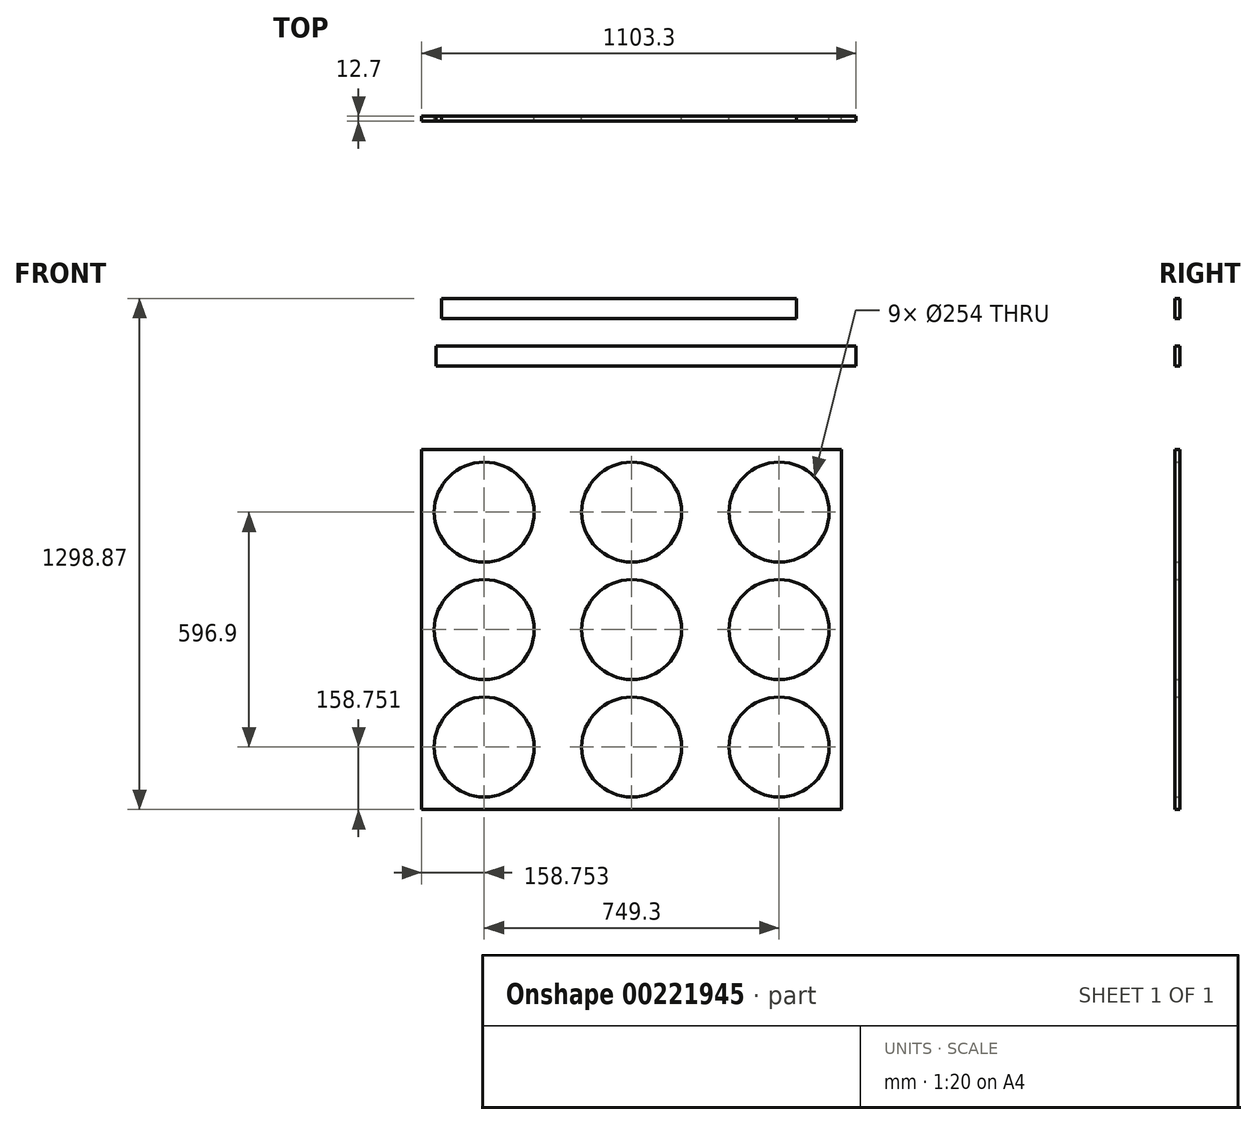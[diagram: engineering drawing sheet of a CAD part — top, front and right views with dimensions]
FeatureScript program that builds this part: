
annotation { "Feature Type Name" : "Feature", "Feature Type Description" : "" }
export const myFeature = defineFeature(function(context is Context, id is Id, definition is map)
    precondition{}
    {
        {
            var Q0;
            Q0=qCreatedBy(makeId("Front.planeOp"),FACE);
            var sketch = newSketch(context, id + "F0", { "sketchPlane" : qUnion([Q0])});
            skLineSegment(sketch, "E0.bottom", {"start": v(-474.18, 572.11) * mm, "end": v(592.62, 572.11) * mm});
            skLineSegment(sketch, "E0.top", {"start": v(-474.18, -342.29) * mm, "end": v(592.62, -342.29) * mm});
            skLineSegment(sketch, "E0.left", {"start": v(-474.18, 572.11) * mm, "end": v(-474.18, -342.29) * mm});
            skLineSegment(sketch, "E0.right", {"start": v(592.62, 572.11) * mm, "end": v(592.62, -342.29) * mm});
            skLineSegment(sketch, "E1.0", {"start": v(-474.18, -183.54) * mm, "end": v(440.22, -183.54) * mm, "construction": true});
            skLineSegment(sketch, "E2.0", {"start": v(-315.43, 572.11) * mm, "end": v(-315.43, -342.29) * mm, "construction": true});
            skLineSegment(sketch, "E3.0", {"start": v(433.87, 572.11) * mm, "end": v(433.87, -342.29) * mm, "construction": true});
            skLineSegment(sketch, "E4.0", {"start": v(-474.18, 114.91) * mm, "end": v(440.22, 114.91) * mm, "construction": true});
            skLineSegment(sketch, "E5.0", {"start": v(59.22, 572.11) * mm, "end": v(59.22, -342.29) * mm, "construction": true});
            skCircle(sketch, "E6", {"center": v(-315.43, 114.91) * mm, "radius": 127 * mm});
            skCircle(sketch, "E7", {"center": v(-315.43, -183.54) * mm, "radius": 127 * mm});
            skCircle(sketch, "E8", {"center": v(433.87, -183.54) * mm, "radius": 127 * mm});
            skCircle(sketch, "E9", {"center": v(433.87, 114.91) * mm, "radius": 127 * mm});
            skLineSegment(sketch, "E10.0", {"start": v(-474.18, 413.36) * mm, "end": v(440.22, 413.36) * mm, "construction": true});
            skCircle(sketch, "E11", {"center": v(-315.43, 413.36) * mm, "radius": 127 * mm});
            skCircle(sketch, "E12", {"center": v(433.87, 413.36) * mm, "radius": 127 * mm});
            skCircle(sketch, "E13", {"center": v(59.22, 413.36) * mm, "radius": 127 * mm});
            skCircle(sketch, "E14", {"center": v(59.22, 114.91) * mm, "radius": 127 * mm});
            skCircle(sketch, "E15", {"center": v(59.22, -183.54) * mm, "radius": 127 * mm});
            skSolve(sketch);
        }
        {
            var Q0;
            Q0=makeQuery(id+"F0.imprint","IMPRINT",FACE,{"disambiguationData":[TD([[makeQuery(id+"F0.imprint","IMPRINT",EDGE,{"derivedFrom":sQuery(id+"F0.wireOp",EDGE,"E0.bottom")}),-1.0]])]});
            extrude(context, id + "F1", {"entities" : qUnion([Q0]), "depth" : 12.7 * mm});
        }
        {
            var Q0;
            Q0=qCreatedBy(makeId("Front.planeOp"),FACE);
            var sketch = newSketch(context, id + "F2", { "sketchPlane" : qUnion([Q0])});
            skLineSegment(sketch, "E16.bottom", {"start": v(-437.68, 835.84) * mm, "end": v(629.12, 835.84) * mm});
            skLineSegment(sketch, "E16.top", {"start": v(-437.68, 785.04) * mm, "end": v(629.12, 785.04) * mm});
            skLineSegment(sketch, "E16.left", {"start": v(-437.68, 835.84) * mm, "end": v(-437.68, 785.04) * mm});
            skLineSegment(sketch, "E16.right", {"start": v(629.12, 835.84) * mm, "end": v(629.12, 785.04) * mm});
            skLineSegment(sketch, "E17.bottom", {"start": v(-423.4, 956.58) * mm, "end": v(478.3, 956.58) * mm});
            skLineSegment(sketch, "E17.top", {"start": v(-423.4, 905.78) * mm, "end": v(478.3, 905.78) * mm});
            skLineSegment(sketch, "E17.left", {"start": v(-423.4, 956.58) * mm, "end": v(-423.4, 905.78) * mm});
            skLineSegment(sketch, "E17.right", {"start": v(478.3, 956.58) * mm, "end": v(478.3, 905.78) * mm});
            skSolve(sketch);
        }
        {
            var Q0;
            Q0=makeQuery(id+"F2.imprint","IMPRINT",FACE,{"disambiguationData":[TD([[makeQuery(id+"F2.imprint","IMPRINT",EDGE,{"derivedFrom":sQuery(id+"F2.wireOp",EDGE,"E17.bottom")}),-1.0]])]});
            var Q1;
            Q1=makeQuery(id+"F2.imprint","IMPRINT",FACE,{"disambiguationData":[TD([[makeQuery(id+"F2.imprint","IMPRINT",EDGE,{"derivedFrom":sQuery(id+"F2.wireOp",EDGE,"E16.bottom")}),-1.0]])]});
            extrude(context, id + "F3", {"entities" : qUnion([Q0, Q1]), "depth" : 12.7 * mm});
        }
    });
